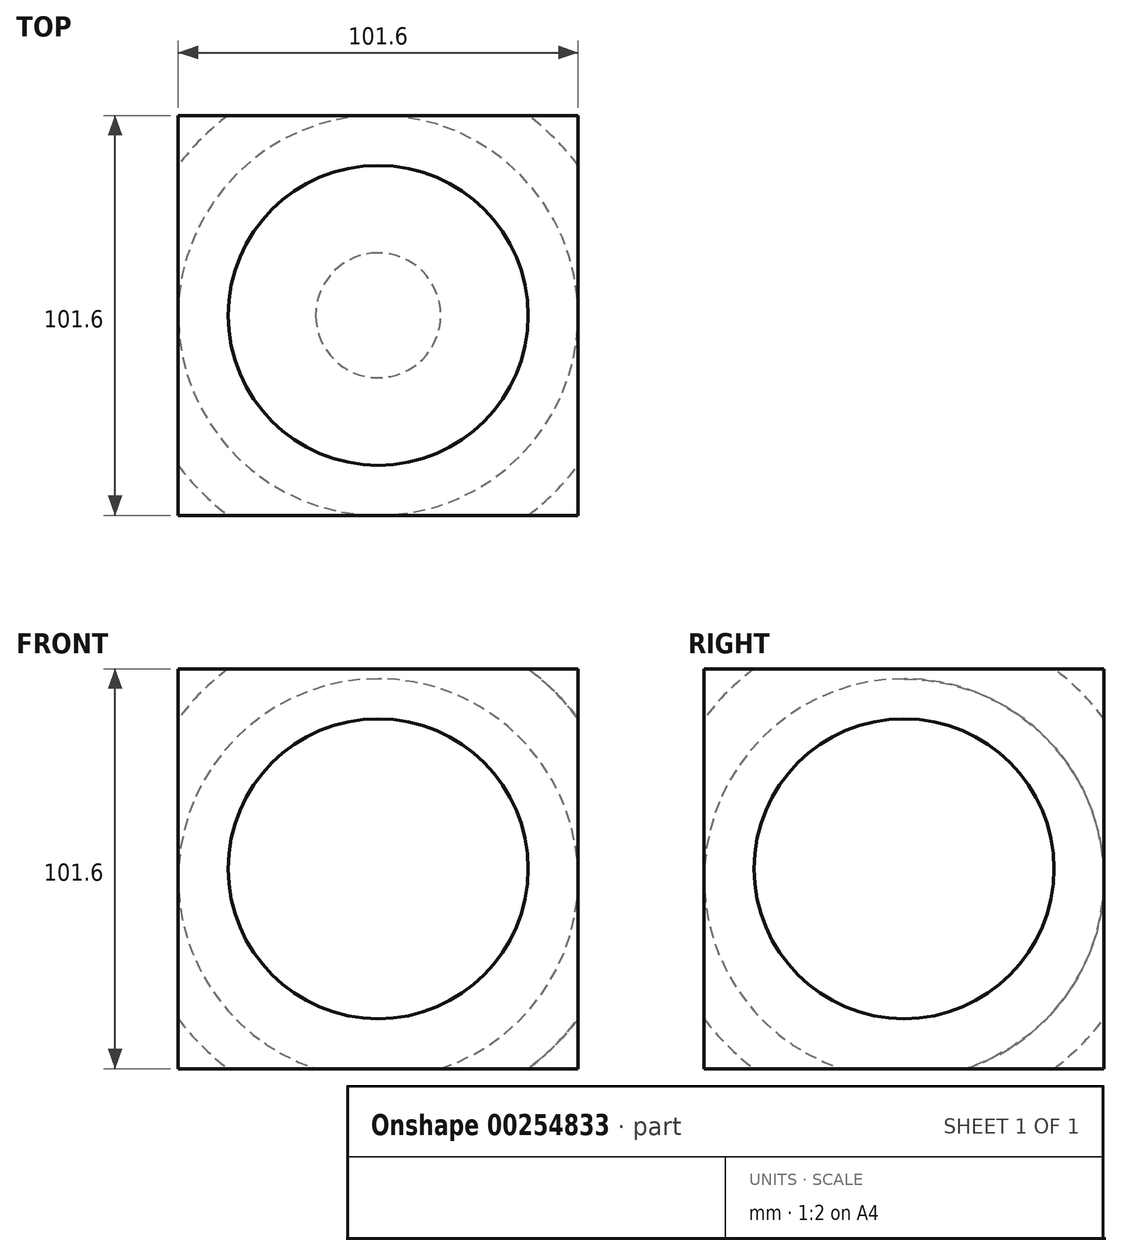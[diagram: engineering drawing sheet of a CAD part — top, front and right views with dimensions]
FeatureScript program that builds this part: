
annotation { "Feature Type Name" : "Feature", "Feature Type Description" : "" }
export const myFeature = defineFeature(function(context is Context, id is Id, definition is map)
    precondition{}
    {
        {
            var Q0;
            Q0=qCreatedBy(makeId("Top.planeOp"),FACE);
            var sketch = newSketch(context, id + "F0", { "sketchPlane" : qUnion([Q0])});
            skLineSegment(sketch, "E0.bottom", {"start": v(50.8, -50.8) * mm, "end": v(-50.8, -50.8) * mm});
            skLineSegment(sketch, "E0.top", {"start": v(50.8, 50.8) * mm, "end": v(-50.8, 50.8) * mm});
            skLineSegment(sketch, "E0.left", {"start": v(50.8, -50.8) * mm, "end": v(50.8, 50.8) * mm});
            skLineSegment(sketch, "E0.right", {"start": v(-50.8, -50.8) * mm, "end": v(-50.8, 50.8) * mm});
            skPoint(sketch, "E0.middle", {"position": v(0, 0) * mm});
            skSolve(sketch);
        }
        {
            var Q0;
            Q0 = qSketchRegion(id + "F0", true);
            extrude(context, id + "F1", {"entities" : qUnion([Q0]), "depth" : 101.6 * mm});
        }
        {
            var Q0;
            Q0=qCreatedBy(makeId("Front.planeOp"),FACE);
            var sketch = newSketch(context, id + "F2", { "sketchPlane" : qUnion([Q0])});
            skPoint(sketch, "E1.center.orphan", {"position": v(0, 50.8) * mm});
            skPoint(sketch, "E2.orphan", {"position": v(0, 101.6) * mm});
            skPoint(sketch, "E3.start.orphan", {"position": v(0, 0) * mm});
            skArc(sketch, "E4", {"start": v(0, -12.7) * mm, "mid": v(63.5, 50.8) * mm, "end": v(0, 114.3) * mm});
            skLineSegment(sketch, "E5", {"start": v(0, 114.3) * mm, "end": v(0, -12.7) * mm});
            skSolve(sketch);
        }
        {
            var Q0;
            Q0 = qSketchRegion(id + "F2", true);
            var Q1;
            Q1=sQuery(id+"F2.wireOp",EDGE,"E5");
            revolve(context, id + "F3", {"operationType" : NewBodyOperationType.REMOVE, "entities" : qUnion([Q0]), "axis" : qUnion([Q1]), "revolveType" : RevolveType.FULL, "oppositeDirection" : true});
        }
        {
            var Q0;
            Q0=qCreatedBy(makeId("Right.planeOp"),FACE);
            var sketch = newSketch(context, id + "F4", { "sketchPlane" : qUnion([Q0])});
            skLineSegment(sketch, "E6", {"start": v(0, 2.54) * mm, "end": v(0, 101.6) * mm});
            skArc(sketch, "E7", {"start": v(15.86, 2.54) * mm, "mid": v(50.16, 58.83) * mm, "end": v(0, 101.6) * mm});
            skLineSegment(sketch, "E8", {"start": v(0, 2.54) * mm, "end": v(15.86, 2.54) * mm});
            skPoint(sketch, "E9.orphan", {"position": v(0, 0) * mm});
            skSolve(sketch);
        }
        {
            var Q0;
            {var subQ0=sQuery(id+"F4.wireOp",EDGE,"E6");Q0=makeQuery(id+"F4.imprint","IMPRINT",FACE,{"disambiguationData":[TD([[makeQuery(id+"F4.imprint","IMPRINT",EDGE,{"derivedFrom":subQ0}),-1.0]])]});}
            var Q1;
            Q1=sQuery(id+"F4.wireOp",EDGE,"E6");
            revolve(context, id + "F5", {"entities" : qUnion([Q0]), "axis" : qUnion([Q1]), "revolveType" : RevolveType.FULL});
        }
        {
            var Q0;
            Q0=makeQuery(id+"F5.opRevolve","SWEPT_BODY",BODY,{"disambiguationData":[OSD([sQuery(id+"F4.wireOp",EDGE,"E6"),sQuery(id+"F4.wireOp",EDGE,"E7"),sQuery(id+"F4.wireOp",EDGE,"E8")])]});
            var Q1;
            Q1=qCreatedBy(makeId("Origin.pointOp"),VERTEX);
            transform(context, id + "F6", {"entities" : qUnion([Q0]), "transformType" : TransformType.TRANSLATION_3D, "dx" : 0 * mm, "dy" : 0 * mm, "dz" : -2.54 * mm, "makeCopy" : false});
        }
    });
